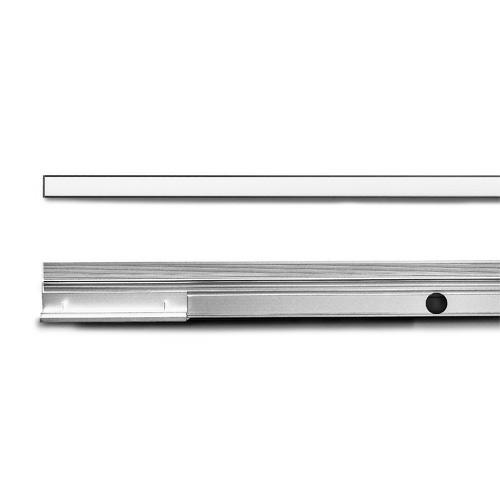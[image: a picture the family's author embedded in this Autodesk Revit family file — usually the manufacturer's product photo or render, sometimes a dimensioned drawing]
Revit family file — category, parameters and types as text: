
# Revit family: SIMES_S.7001W_Continuous line
name_source: partatom
category: Lighting Fixtures
revit_build: Autodesk Revit 2016 (Build: 20150714_1515(x64)
units: mm (PartAtom-declared; Revit-internal decimal feet)

## family parameters
Cut with Voids When Loaded = No
Host = Face
Light Source = Yes
OmniClass Number = 23.80.70.14
OmniClass Title = Luminaries for External Lighting
Part Type = Normal
Room Calculation Point = No
Round Connector Dimension = Use Diameter
Shared = No

## types (1)
- SIMES_S.7001W_Continuous line
    Approval mark = CE
    Assembly Code = D5020
    Color Filter = 16777215
    Color Rendering Index = CRI 80
    Colour Temperature = 3000
    Control Gear = none
    Default Elevation = 1219 mm
    Description = CONTINUOUS LINE 1m
Art. S.7001W
MODULES LED 3000K  24V CRI 80
Rated luminaire luminous flux: 202lm
Rated input power: 7W
Luminaire efficacy: 29lm/W
Without trasformer
CE

PRODUCT TYPE
Inground walk over fitting. Recessing depth 90 mm. IP rating IP 67
MATERIAL CHARACTERISTICS
Fixing base and recessing box in extruded anodized EN AW-6060 aluminium housing (copper free) with high corrosion resistance. Mechanical resistance IK 09 Maximum load capacity 500 Kg
LIGHTING PERFORMANCE
Extruded polycarbonate diffuser 3mm thick. Lamp  fixed position. LOR -- 
LOW SURFACE TEMPERATURE
Surface temperature of diffusor 39°C (Ta 25°C)
RECESSING BOX
The housing is realized in aluminium and it is supplied with a protective cover resistant to tearing, which is to be removed only after cementing the housing flush to the pavement, just before the final installation of the fitting.
WIRING
CONTINUOUS LINE is equipped with to-be-fixed supports to perfectly align additional fittings and provide easy installation. Using this simple system to join the housing and supports also assists in levelling the housings in a CONTINUOUS LINE. It is possible to level the fitting using screws. The wiring is external to the housing . Luminaire hard wired with 0,15m H05RN-F single cable. The result is a continuous line of light. Isolation: CLASS III . Available colours: Anodized aluminium (cod.13). Weight: 3.4 Kg Glow Wire test: 850°C
Lamp included.
LINEA CONTINUA PATENTED 2013
This luminaire contains built-in LED modules with energy class: A, A+, A++. In case of damage or malfunction please contact the manufacturer to receive additional instructions on how to replace and relative spare parts to order. The LED modules cannot be handled in the luminaire by the end user (Regulation UE 874/2012).
LED circuit boards are engineered accordingly to actual Lumen Maintenance regulation (LM80) and Technical Memorandum (TM21) where uniformity and quality of light is 50.000 hours referred to L70  B20 Ta 25°C.Lifecycle refers to LED circuit boards only, all others components of the luminaire are excluded.
    Dimming Lamp Color Temperature Shift = <None>
    IFC Classification = Light Fixture
    IK Rating = IK 09
    Lamp = LED
    Lamp Light Flux = 740
    Lamp count = 1
    Last Update = 02/08/2018 10:06:51
    Lifetime = 50000 L70 B20 Ta 25°C
    Light Output Ratio = 100
    Luminous efficacy = 28,9
    Manufacturer = SIMES
    Masterformat 2014 Code = 26 56 00
    Masterformat 2014 Description = Exterior Lighting
    Model = S.7001W
    Mounting Place = Floor
    Mounting Type = Recessed
    NBS Reference Code = 49
    NBS Reference Description = Luminaries And Lamps
    OmniClass Code = 23-35 47 11
    OmniClass Description = Lighting Fixture
    Photometric Web File = S7001W.ies
    Product Group = floor-recessed luminaires
    Product Name = Continuous line
    Protection Class = Safety extra-low voltage
    Protection Degree = IP 67
    System Light Flux = 202
    System Power = 7
    Tilt Angle = 90.00°
    Type Comments = SIMES S.p.A. - All rights reserved
    Type Image = lineacontinua1m.jpg
    UNSPSC Code = 3911
    URL = http://www.simes.it
    Uniclass 1.4 Code = YJ73
    Uniclass 1.4 Description = Luminaries and lamps
    Uniclass 2.0 Code = PR-49
    Uniclass 2.0 Description = Luminaries and lamps
    Uniclass 2015 Code = EF_70_80
    Uniclass 2015 Name = Lighting
    Uniformat II Code = D5020
    Uniformat II Description = Lighting & Branch Wiring
    Voltage = 24V
    Wattage Comments = 10W
